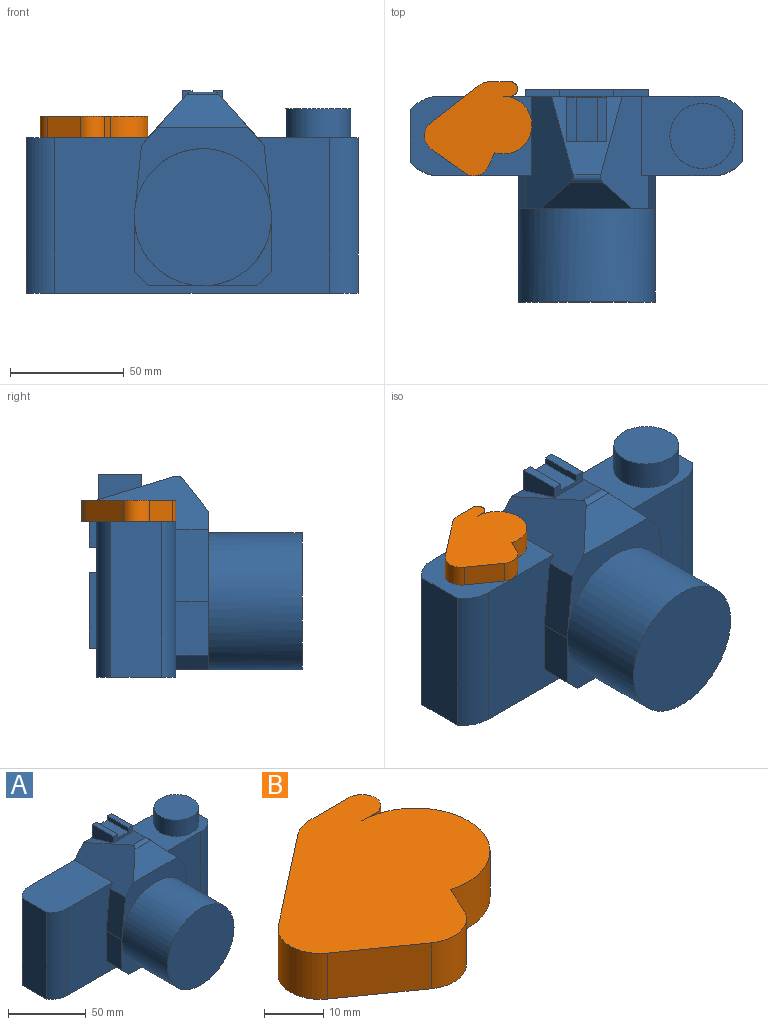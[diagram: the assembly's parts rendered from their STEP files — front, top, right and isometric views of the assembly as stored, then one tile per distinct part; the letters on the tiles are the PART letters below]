
ASSEMBLY  parts=2 mates=1
PART A: 61 faces, bbox 146.1x93.7x88.9 mm
  f0: plane 19.05x9.53mm, normal (0,0,1), area 181.5mm2, adj f53,f55,f57,f59
  f1: plane 34.45x31.12mm, normal (0,0.29,0.96), area 433mm2, adj f6,f23,f24,f52,f53,f54,f55,f56
  f2: plane 59.13x33.71mm, normal (0,-1,0), area 758.4mm2, adj f15,f21,f23,f24,f26,f51
  f3: plane 30.16x30.16mm, normal (0,-1,0), area 175.1mm2, adj f16,f17,f18,f26
  f4: plane 44.13x34.93mm, normal (0,0,1), area 851.5mm2, adj f5,f6,f10,f11,f12,f24,f29
  f5: cylinder r=15.88mm len=68.26mm, axis (0,0,-1), area 1004.9mm2, adj f4,f6,f12,f14
  f6: plane 120.65x77.79mm, normal (0,1,0), area 6398.7mm2, adj f1,f4,f5,f7,f13,f14,f23,f24
  f7: cylinder r=15.88mm len=68.26mm, axis (0,0,-1), area 1004.9mm2, adj f6,f8,f13,f14
  f8: plane 68.26x22.23mm, normal (-1,0,0), area 1517.1mm2, adj f7,f9,f13,f14
  f9: cylinder r=15.88mm len=68.26mm, axis (0,0,-1), area 1004.9mm2, adj f8,f10,f13,f14
  f10: plane 120.65x68.26mm, normal (0,-1,0), area 4479.8mm2, adj f4,f9,f11,f13,f14,f15,f16,f17
  f11: cylinder r=15.88mm len=68.26mm, axis (0,0,-1), area 1004.9mm2, adj f4,f10,f12,f14
  f12: plane 68.26x22.23mm, normal (1,0,0), area 1517.1mm2, adj f4,f5,f11,f14
  f13: plane 53.66x34.93mm, normal (0,0,1), area 1825.4mm2, adj f6,f7,f8,f9,f10,f23
  f14: plane 146.05x34.93mm, normal (0,0,-1), area 5003.7mm2, adj f5,f6,f7,f8,f9,f10,f11,f12
  f15: plane 31.75x14.29mm, normal (-1,0,0.1), area 455.9mm2, adj f2,f10,f16,f23,f28
  f16: plane 23.81x14.29mm, normal (-1,0,0), area 340.2mm2, adj f3,f10,f15,f17
  f17: plane 14.29x6.35mm, normal (-0.71,0,-0.71), area 128.3mm2, adj f3,f10,f16,f18
  f18: plane 47.63x14.29mm, normal (0,0,-1), area 680.4mm2, adj f3,f10,f17,f19,f22
  f19: plane 14.29x6.35mm, normal (0.71,0,-0.71), area 128.3mm2, adj f10,f18,f20,f22
  f20: plane 23.81x14.29mm, normal (1,0,0), area 340.2mm2, adj f10,f19,f21,f22
  f21: plane 31.75x14.29mm, normal (1,0,0.1), area 455.9mm2, adj f2,f10,f20,f24,f25
  f22: plane 30.16x30.16mm, normal (0,-1,0), area 175.1mm2, adj f18,f19,f20,f26
  f23: plane 49.21x23.32mm, normal (-0.74,0,0.67), area 1017.7mm2, adj f1,f2,f6,f10,f13,f15,f51,f52
  f24: plane 49.21x23.32mm, normal (0.74,0,0.67), area 1017.7mm2, adj f1,f2,f4,f6,f10,f21,f51,f52
  f25: plane 5.97x0.6mm, normal (0,1,0), area 0.6mm2, adj f21,f26
  f26: cylinder r=30.16mm len=60.33mm, axis (0,1,0), area 7822.3mm2, adj f2,f3,f22,f25,f27,f28
  f27: plane 60.33x60.33mm, normal (0,-1,0), area 2858.1mm2, adj f26
  f28: plane 5.97x0.6mm, normal (0,1,0), area 0.6mm2, adj f15,f26
  f29: cylinder r=14.29mm len=28.58mm, axis (0,0,-1), area 1140.1mm2, adj f4,f30
  f30: plane 28.58x28.58mm, normal (0,0,1), area 641.3mm2, adj f29
  f31: plane 53.98x3.18mm, normal (0,0,-1), area 171.4mm2, adj f6,f32,f38,f39
  f32: plane 33.34x3.18mm, normal (-1,0,0), area 105.8mm2, adj f6,f31,f33,f39
  f33: plane 53.98x3.18mm, normal (0,0,1), area 171.4mm2, adj f6,f32,f38,f39
  f34: plane 23.81x3.18mm, normal (1,0,0), area 75.6mm2, adj f35,f37,f39,f40
  f35: plane 31.75x3.18mm, normal (0,0,1), area 100.8mm2, adj f34,f36,f39,f40
  f36: plane 23.81x3.18mm, normal (-1,0,0), area 75.6mm2, adj f35,f37,f39,f40
  f37: plane 31.75x3.18mm, normal (0,0,-1), area 100.8mm2, adj f34,f36,f39,f40
  f38: plane 33.34x3.18mm, normal (1,0,0), area 105.8mm2, adj f6,f31,f33,f39
  f39: plane 53.98x33.34mm, normal (0,1,0), area 1043.3mm2, adj f31,f32,f33,f34,f35,f36,f37,f38
  f40: plane 31.75x23.81mm, normal (0,1,0), area 756mm2, adj f34,f35,f36,f37
  f41: plane 23.81x3.18mm, normal (0,0,-1), area 75.6mm2, adj f6,f42,f48,f49
  f42: plane 17.46x3.18mm, normal (-1,0,0), area 55.4mm2, adj f6,f41,f43,f49
  f43: plane 23.81x3.18mm, normal (0,0,1), area 75.6mm2, adj f6,f42,f48,f49
  f44: plane 17.46x3.18mm, normal (0,0,1), area 55.4mm2, adj f45,f47,f49,f50
  f45: plane 11.11x3.18mm, normal (-1,0,0), area 35.3mm2, adj f44,f46,f49,f50
  f46: plane 17.46x3.18mm, normal (0,0,-1), area 55.4mm2, adj f45,f47,f49,f50
  f47: plane 11.11x3.18mm, normal (1,0,0), area 35.3mm2, adj f44,f46,f49,f50
  f48: plane 17.46x3.18mm, normal (1,0,0), area 55.4mm2, adj f6,f41,f43,f49
  f49: plane 23.81x17.46mm, normal (0,1,0), area 221.8mm2, adj f41,f42,f43,f44,f45,f46,f47,f48
  f50: plane 17.46x11.11mm, normal (0,1,0), area 194.1mm2, adj f44,f45,f46,f47
  f51: plane 39.69x14.19mm, normal (0,-0.78,0.62), area 489.2mm2, adj f2,f23,f24,f52
  f52: cylinder r=3.17mm len=14.14mm, axis (1,0,0), area 47.5mm2, adj f1,f23,f24,f51
  f53: plane 17.46x5.07mm, normal (0,-1,0), area 58.3mm2, adj f0,f1,f54,f56,f57,f58,f59,f60
  f54: plane 19.05x10.87mm, normal (1,0,0), area 151.9mm2, adj f1,f53,f55,f60
  f55: plane 17.46x10.87mm, normal (0,1,0), area 159.6mm2, adj f0,f1,f54,f56,f57,f58,f59,f60
  f56: plane 19.05x10.87mm, normal (-1,0,0), area 151.9mm2, adj f1,f53,f55,f58
  f57: plane 19.05x3.18mm, normal (1,0,0), area 60.5mm2, adj f0,f53,f55,f58
  f58: plane 19.05x3.97mm, normal (0,0,1), area 75.6mm2, adj f53,f55,f56,f57
  f59: plane 19.05x3.18mm, normal (-1,0,0), area 60.5mm2, adj f0,f53,f55,f60
  f60: plane 19.05x3.97mm, normal (0,0,1), area 75.6mm2, adj f53,f54,f55,f59
PART B: 12 faces, bbox 47.3x41.3x9.5 mm
  f0: plane 9.53x5.94mm, normal (0.91,-0.42,0), area 62.4mm2, adj f1,f9,f10,f11
  f1: cylinder r=12.7mm len=25.4mm, axis (0,0,-1), area 415.3mm2, adj f0,f2,f10,f11
  f2: plane 9.53x3.18mm, normal (0,-1,0), area 30.2mm2, adj f1,f3,f10,f11
  f3: cylinder r=3.17mm len=9.53mm, axis (0,0,-1), area 95mm2, adj f2,f4,f10,f11
  f4: plane 9.53x9.53mm, normal (0,1,0), area 90.7mm2, adj f3,f5,f10,f11
  f5: cylinder r=7.81mm len=9.53mm, axis (0,0,-1), area 44.9mm2, adj f4,f6,f10,f11
  f6: plane 21.17x16.54mm, normal (-0.62,0.79,0), area 255.9mm2, adj f5,f7,f10,f11
  f7: cylinder r=7.14mm len=11.46mm, axis (0,0,-1), area 126.7mm2, adj f6,f8,f10,f11
  f8: plane 14.57x10.32mm, normal (-0.58,-0.82,0), area 170mm2, adj f7,f9,f10,f11
  f9: cylinder r=7.14mm len=10.6mm, axis (0,0,-1), area 119.1mm2, adj f0,f8,f10,f11
  f10: plane 47.31x41.28mm, normal (0,0,1), area 1251.9mm2, adj f0,f1,f2,f3,f4,f5,f6,f7
  f11: plane 47.31x41.28mm, normal (0,0,-1), area 1251.9mm2, adj f0,f1,f2,f3,f4,f5,f6,f7
PLACE A at identity
PLACE B at identity
MATE fastened B.f1 <-> A.f13  axis (0,0,-1) through (-32.07,4.76,68.26)mm
